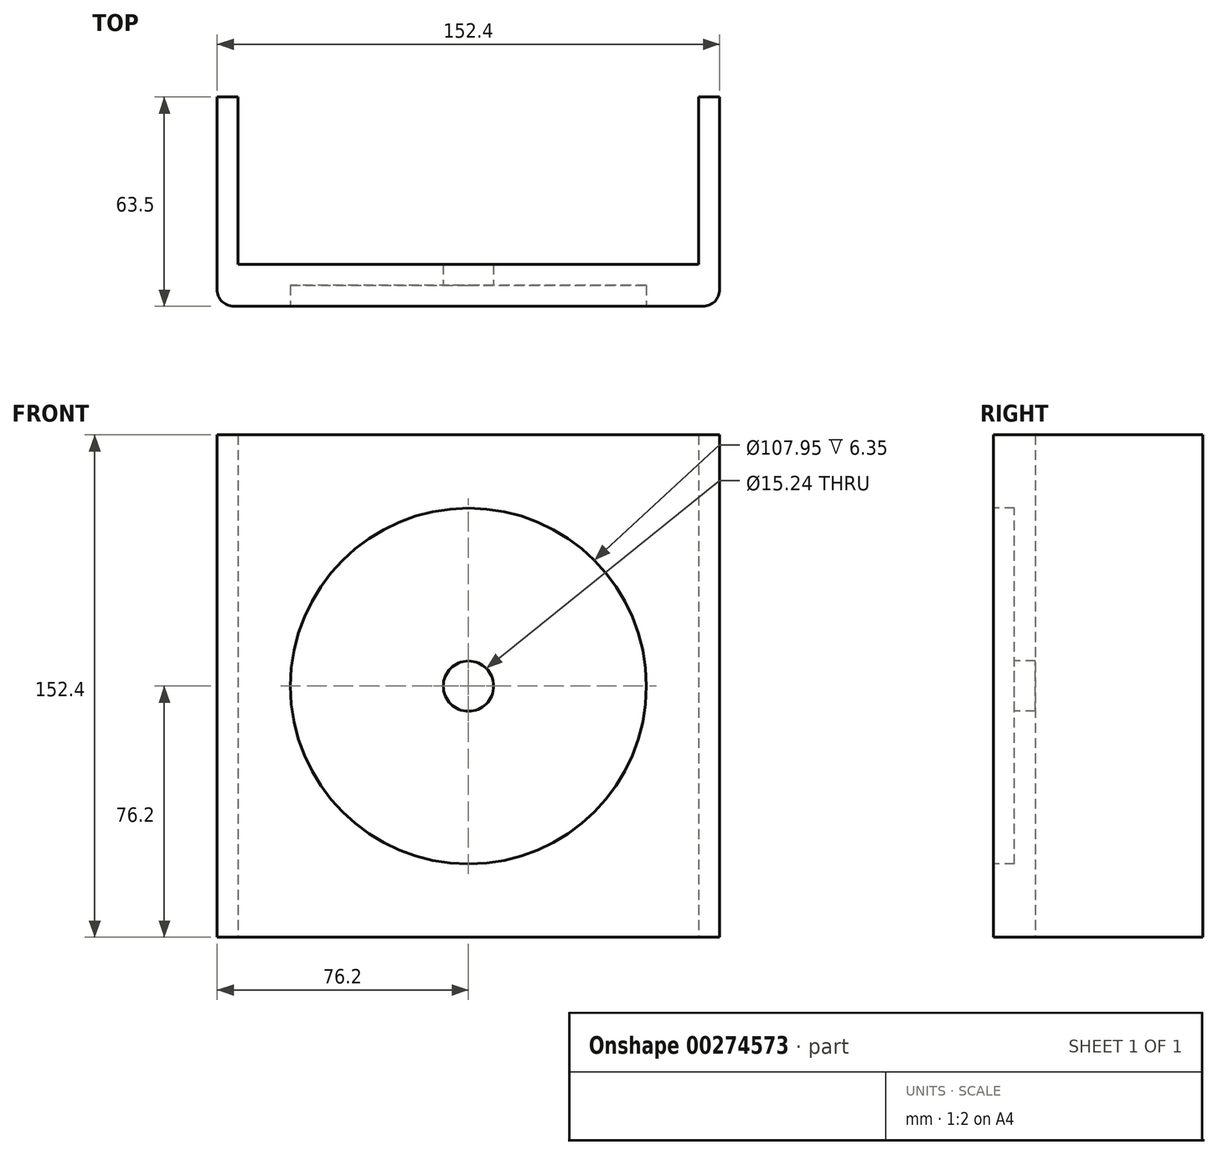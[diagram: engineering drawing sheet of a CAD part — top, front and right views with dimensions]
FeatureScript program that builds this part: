
annotation { "Feature Type Name" : "Feature", "Feature Type Description" : "" }
export const myFeature = defineFeature(function(context is Context, id is Id, definition is map)
    precondition{}
    {
        {
            var Q0;
            Q0=qCreatedBy(makeId("Front.planeOp"),FACE);
            var sketch = newSketch(context, id + "F0", { "sketchPlane" : qUnion([Q0])});
            skLineSegment(sketch, "E0.bottom", {"start": v(0, 0) * mm, "end": v(-152.4, 0) * mm});
            skLineSegment(sketch, "E0.top", {"start": v(0, 152.4) * mm, "end": v(-152.4, 152.4) * mm});
            skLineSegment(sketch, "E0.left", {"start": v(0, 0) * mm, "end": v(0, 152.4) * mm});
            skLineSegment(sketch, "E0.right", {"start": v(-152.4, 0) * mm, "end": v(-152.4, 152.4) * mm});
            skSolve(sketch);
        }
        {
            var Q0;
            Q0=makeQuery(id+"F0.imprint","IMPRINT",FACE,{"disambiguationData":[TD([[makeQuery(id+"F0.imprint","IMPRINT",EDGE,{"derivedFrom":sQuery(id+"F0.wireOp",EDGE,"E0.bottom")}),-1.0]])]});
            extrude(context, id + "F1", {"entities" : qUnion([Q0]), "depth" : 12.7 * mm});
        }
        {
            var Q0;
            Q0=makeQuery(id+"F1.opExtrude","CAP_FACE",FACE,{"disambiguationData":[OSD([sQuery(id+"F0.wireOp",EDGE,"E0.bottom"),sQuery(id+"F0.wireOp",EDGE,"E0.top"),sQuery(id+"F0.wireOp",EDGE,"E0.left"),sQuery(id+"F0.wireOp",EDGE,"E0.right")])],"isStart":false});
            var sketch = newSketch(context, id + "F2", { "sketchPlane" : qUnion([Q0])});
            skCircle(sketch, "E1", {"center": v(-76.2, 76.2) * mm, "radius": 53.98 * mm});
            skSolve(sketch);
        }
        {
            var Q0;
            Q0=makeQuery(id+"F2.imprint","IMPRINT",FACE,{"disambiguationData":[TD([[makeQuery(id+"F2.imprint","IMPRINT",EDGE,{"derivedFrom":sQuery(id+"F2.wireOp",EDGE,"E1")}),1.0]])]});
            extrude(context, id + "F3", {"entities" : qUnion([Q0]), "operationType" : NewBodyOperationType.REMOVE, "oppositeDirection" : true, "depth" : 6.35 * mm});
        }
        {
            var Q0;
            Q0=makeQuery(id+"F1.opExtrude","SWEPT_FACE",FACE,{"disambiguationData":[OSD([sQuery(id+"F0.wireOp",EDGE,"E0.bottom")])]});
            var sketch = newSketch(context, id + "F4", { "sketchPlane" : qUnion([Q0])});
            skLineSegment(sketch, "E2.bottom", {"start": v(-152.4, 0) * mm, "end": v(-146.05, 0) * mm});
            skLineSegment(sketch, "E2.top", {"start": v(-152.4, -50.8) * mm, "end": v(-146.05, -50.8) * mm});
            skLineSegment(sketch, "E2.left", {"start": v(-152.4, 0) * mm, "end": v(-152.4, -50.8) * mm});
            skLineSegment(sketch, "E2.right", {"start": v(-146.05, 0) * mm, "end": v(-146.05, -50.8) * mm});
            skLineSegment(sketch, "E3.bottom", {"start": v(0, 0) * mm, "end": v(-6.35, 0) * mm});
            skLineSegment(sketch, "E3.top", {"start": v(0, -50.8) * mm, "end": v(-6.35, -50.8) * mm});
            skLineSegment(sketch, "E3.left", {"start": v(0, 0) * mm, "end": v(0, -50.8) * mm});
            skLineSegment(sketch, "E3.right", {"start": v(-6.35, 0) * mm, "end": v(-6.35, -50.8) * mm});
            skSolve(sketch);
        }
        {
            var Q0;
            Q0=makeQuery(id+"F4.imprint","IMPRINT",FACE,{"disambiguationData":[TD([[makeQuery(id+"F4.imprint","IMPRINT",EDGE,{"derivedFrom":sQuery(id+"F4.wireOp",EDGE,"E2.bottom")}),1.0]])]});
            var Q1;
            Q1=makeQuery(id+"F4.imprint","IMPRINT",FACE,{"disambiguationData":[TD([[makeQuery(id+"F4.imprint","IMPRINT",EDGE,{"derivedFrom":sQuery(id+"F4.wireOp",EDGE,"E3.bottom")}),1.0]])]});
            extrude(context, id + "F5", {"entities" : qUnion([Q0, Q1]), "operationType" : NewBodyOperationType.ADD, "oppositeDirection" : true, "depth" : 152.4 * mm});
        }
        {
            var Q0;
            Q0=makeQuery(id+"F3.boolean.opBoolean","COPY",FACE,{"derivedFrom":makeQuery(id+"F3.opExtrude","CAP_FACE",FACE,{"disambiguationData":[OSD([sQuery(id+"F2.wireOp",EDGE,"E1")])],"isStart":false})});
            var sketch = newSketch(context, id + "F6", { "sketchPlane" : qUnion([Q0])});
            skCircle(sketch, "E4", {"center": v(-76.2, 76.2) * mm, "radius": 7.62 * mm});
            skSolve(sketch);
        }
        {
            var Q0;
            Q0=makeQuery(id+"F6.imprint","IMPRINT",FACE,{"disambiguationData":[TD([[makeQuery(id+"F6.imprint","IMPRINT",EDGE,{"derivedFrom":sQuery(id+"F6.wireOp",EDGE,"E4")}),1.0]])]});
            extrude(context, id + "F7", {"entities" : qUnion([Q0]), "operationType" : NewBodyOperationType.REMOVE, "oppositeDirection" : true, "depth" : 25.4 * mm});
        }
        {
            var Q0;
            Q0=makeQuery(id+"F1.opExtrude","CAP_EDGE",EDGE,{"disambiguationData":[OSD([sQuery(id+"F0.wireOp",EDGE,"E0.right")])],"isStart":false});
            fillet(context, id + "F8", {"entities" : qUnion([Q0]), "radius" : 5.08 * mm, "tangentPropagation" : true, "allowEdgeOverflow" : false});
        }
        {
            var Q0;
            Q0=makeQuery(id+"F1.opExtrude","CAP_EDGE",EDGE,{"disambiguationData":[OSD([sQuery(id+"F0.wireOp",EDGE,"E0.left")])],"isStart":false});
            fillet(context, id + "F9", {"entities" : qUnion([Q0]), "radius" : 5.08 * mm, "tangentPropagation" : true, "allowEdgeOverflow" : false});
        }
    });
